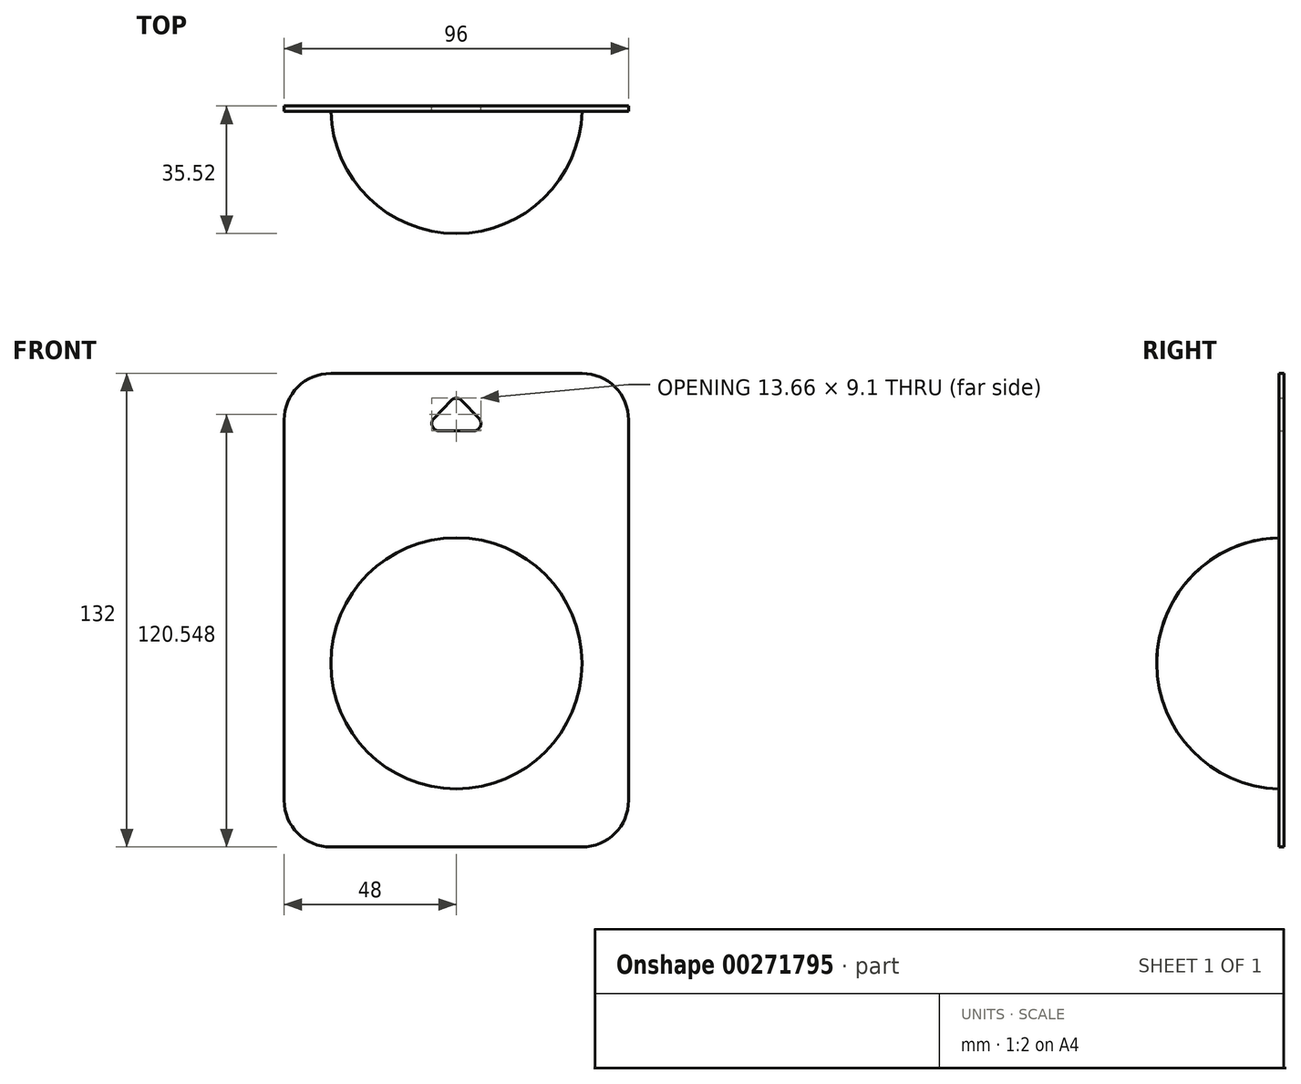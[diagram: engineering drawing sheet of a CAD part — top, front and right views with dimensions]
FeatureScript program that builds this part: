
annotation { "Feature Type Name" : "Feature", "Feature Type Description" : "" }
export const myFeature = defineFeature(function(context is Context, id is Id, definition is map)
    precondition{}
    {
        {
            var Q0;
            Q0=qCreatedBy(makeId("Front.planeOp"),FACE);
            var sketch = newSketch(context, id + "F0", { "sketchPlane" : qUnion([Q0])});
            skLineSegment(sketch, "E0.bottom", {"start": v(35, 66) * mm, "end": v(-35, 66) * mm});
            skLineSegment(sketch, "E0.top", {"start": v(35, -66) * mm, "end": v(-35, -66) * mm});
            skLineSegment(sketch, "E0.left", {"start": v(48, 53) * mm, "end": v(48, -53) * mm});
            skLineSegment(sketch, "E0.right", {"start": v(-48, 53) * mm, "end": v(-48, -53) * mm});
            skPoint(sketch, "E0.middle", {"position": v(0, 0) * mm});
            skPoint(sketch, "E1.visualSharp", {"position": v(-48, 66) * mm});
            skArc(sketch, "E1.filletArc", {"start": v(-35, 66) * mm, "mid": v(-44.2, 62.2) * mm, "end": v(-48, 53) * mm});
            skPoint(sketch, "E2.visualSharp", {"position": v(48, 66) * mm});
            skArc(sketch, "E2.filletArc", {"start": v(48, 53) * mm, "mid": v(44.2, 62.2) * mm, "end": v(35, 66) * mm});
            skPoint(sketch, "E3.visualSharp", {"position": v(48, -66) * mm});
            skArc(sketch, "E3.filletArc", {"start": v(35, -66) * mm, "mid": v(44.2, -62.2) * mm, "end": v(48, -53) * mm});
            skPoint(sketch, "E4.visualSharp", {"position": v(-48, -66) * mm});
            skArc(sketch, "E4.filletArc", {"start": v(-48, -53) * mm, "mid": v(-44.2, -62.2) * mm, "end": v(-35, -66) * mm});
            skLineSegment(sketch, "E5", {"start": v(-1.45, 58.47) * mm, "end": v(-6.3, 53.38) * mm});
            skLineSegment(sketch, "E6", {"start": v(-4.84, 50) * mm, "end": v(0, 50) * mm});
            skLineSegment(sketch, "E7.MirrorCS", {"start": v(1.45, 58.47) * mm, "end": v(6.3, 53.38) * mm});
            skLineSegment(sketch, "E8.MirrorCS", {"start": v(4.84, 50) * mm, "end": v(0, 50) * mm});
            skPoint(sketch, "E9.visualSharp", {"position": v(-9.5, 50) * mm});
            skArc(sketch, "E9.filletArc", {"start": v(-6.3, 53.38) * mm, "mid": v(-6.68, 51.21) * mm, "end": v(-4.84, 50) * mm});
            skPoint(sketch, "E10.visualSharp", {"position": v(9.5, 50) * mm});
            skArc(sketch, "E10.filletArc", {"start": v(4.84, 50) * mm, "mid": v(6.68, 51.21) * mm, "end": v(6.3, 53.38) * mm});
            skPoint(sketch, "E11.visualSharp", {"position": v(0, 60) * mm});
            skArc(sketch, "E11.filletArc", {"start": v(1.45, 58.47) * mm, "mid": v(0, 59.1) * mm, "end": v(-1.45, 58.47) * mm});
            skSolve(sketch);
        }
        {
            var Q0;
            Q0 = qSketchRegion(id + "F0", true);
            extrude(context, id + "F1", {"entities" : qUnion([Q0]), "depth" : 1.5 * mm});
        }
        {
            var Q0;
            Q0=makeQuery(id+"F1.opExtrude","CAP_FACE",FACE,{"disambiguationData":[OSD([sQuery(id+"F0.wireOp",EDGE,"E0.bottom"),sQuery(id+"F0.wireOp",EDGE,"E0.top"),sQuery(id+"F0.wireOp",EDGE,"E0.left"),sQuery(id+"F0.wireOp",EDGE,"E0.right"),sQuery(id+"F0.wireOp",EDGE,"E1.filletArc"),sQuery(id+"F0.wireOp",EDGE,"E2.filletArc"),sQuery(id+"F0.wireOp",EDGE,"E3.filletArc"),sQuery(id+"F0.wireOp",EDGE,"E4.filletArc"),sQuery(id+"F0.wireOp",EDGE,"E5"),sQuery(id+"F0.wireOp",EDGE,"E6"),sQuery(id+"F0.wireOp",EDGE,"E7.MirrorCS"),sQuery(id+"F0.wireOp",EDGE,"E8.MirrorCS"),sQuery(id+"F0.wireOp",EDGE,"E9.filletArc"),sQuery(id+"F0.wireOp",EDGE,"E10.filletArc"),sQuery(id+"F0.wireOp",EDGE,"E11.filletArc")])],"isStart":false});
            var sketch = newSketch(context, id + "F2", { "sketchPlane" : qUnion([Q0])});
            skCircle(sketch, "E12", {"center": v(0, -14.79) * mm, "radius": 35 * mm});
            skSolve(sketch);
        }
        {
            var Q0;
            Q0=qCreatedBy(makeId("Right.planeOp"),FACE);
            var sketch = newSketch(context, id + "F3", { "sketchPlane" : qUnion([Q0])});
            skLineSegment(sketch, "E13.0", {"start": v(-1.5, -14.79) * mm, "end": v(-1.5, 20.21) * mm});
            skArc(sketch, "E14", {"start": v(-1.5, 20.21) * mm, "mid": v(-25.62, 9.62) * mm, "end": v(-35.52, -14.79) * mm});
            skLineSegment(sketch, "E15", {"start": v(-35.52, -14.79) * mm, "end": v(-1.5, -14.79) * mm});
            skPoint(sketch, "E16.orphan", {"position": v(-1.5, -49.79) * mm});
            skSolve(sketch);
        }
        {
            var Q0;
            Q0 = qSketchRegion(id + "F3", true);
            var Q1;
            Q1=sQuery(id+"F3.wireOp",EDGE,"E15");
            revolve(context, id + "F4", {"operationType" : NewBodyOperationType.ADD, "entities" : qUnion([Q0]), "axis" : qUnion([Q1]), "revolveType" : RevolveType.FULL});
        }
    });
